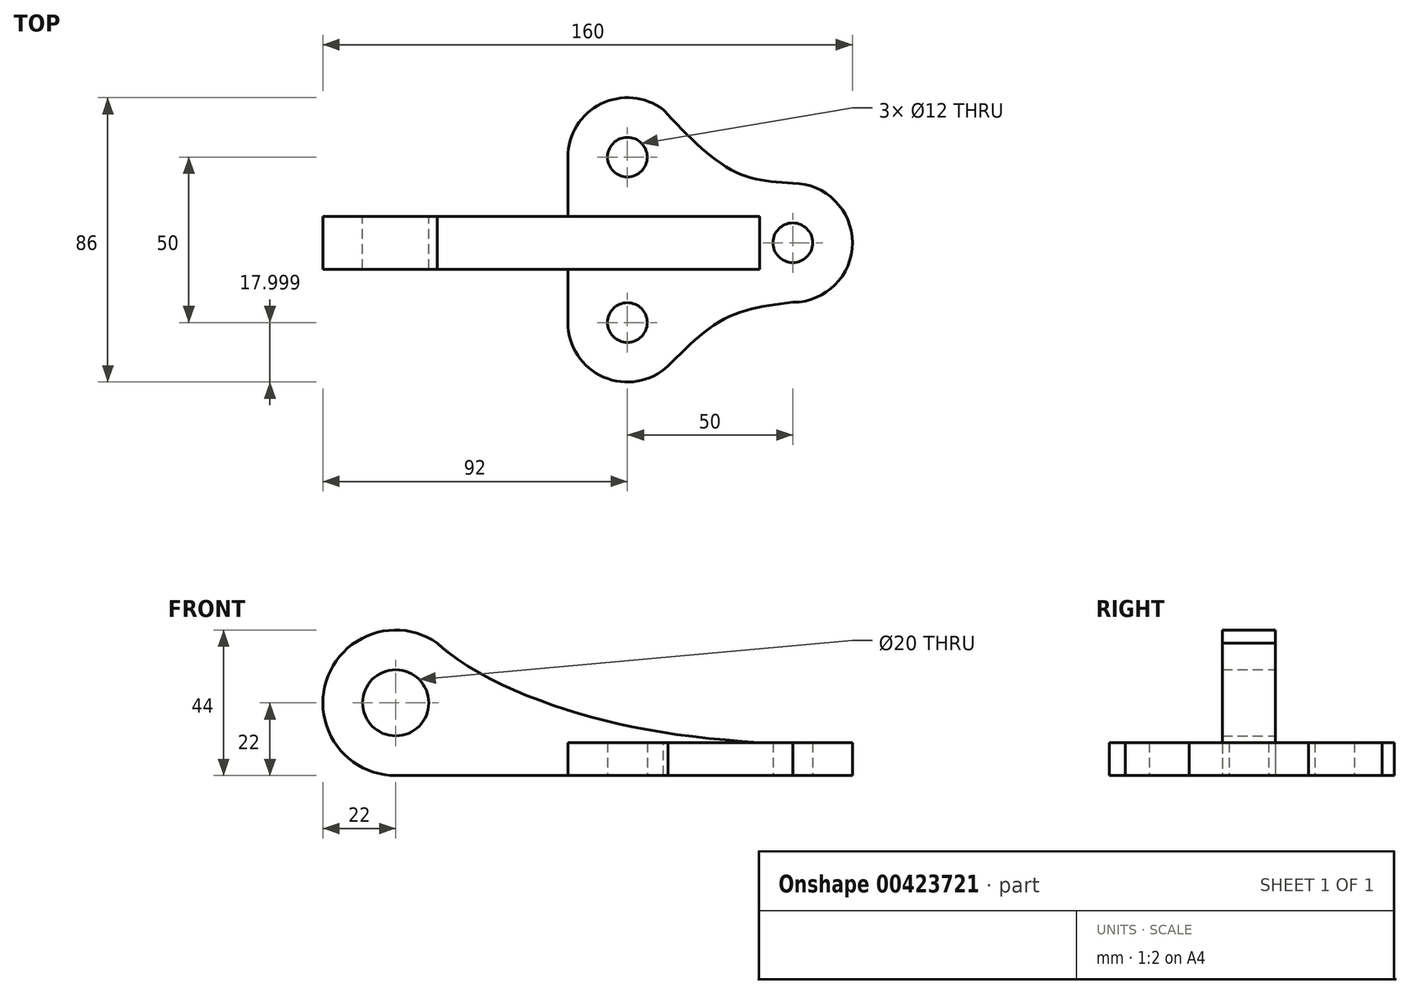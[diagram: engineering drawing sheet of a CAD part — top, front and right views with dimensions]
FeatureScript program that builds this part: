
annotation { "Feature Type Name" : "Feature", "Feature Type Description" : "" }
export const myFeature = defineFeature(function(context is Context, id is Id, definition is map)
    precondition{}
    {
        {
            var Q0;
            Q0=qCreatedBy(makeId("Top.planeOp"),FACE);
            var sketch = newSketch(context, id + "F0", { "sketchPlane" : qUnion([Q0])});
            skCircle(sketch, "E0", {"center": v(0, 25.88) * mm, "radius": 6 * mm});
            skCircle(sketch, "E1", {"center": v(0, -24.12) * mm, "radius": 6 * mm});
            skCircle(sketch, "E2", {"center": v(50, 0) * mm, "radius": 6 * mm});
            skArc(sketch, "E3", {"start": v(15.04, 35.78) * mm, "mid": v(-5.17, 43.12) * mm, "end": v(-18, 25.88) * mm});
            skArc(sketch, "E4", {"start": v(-18, -24.12) * mm, "mid": v(-6.53, -40.9) * mm, "end": v(13.27, -36.29) * mm});
            skArc(sketch, "E5", {"start": v(50.04, -18) * mm, "mid": v(68, 0) * mm, "end": v(50.04, 18) * mm});
            skLineSegment(sketch, "E6", {"start": v(-18, 25.88) * mm, "end": v(-18, -24.12) * mm});
            skFitSpline(sketch, "E7", {"points": [v(10.85, 40.24) * mm, v(31.96, 21.78) * mm, v(50.04, 18) * mm], "startDerivative": vector(37.97, -41.15) * mm, "endDerivative": vector(44.65, -2.57) * mm});
            skFitSpline(sketch, "E8", {"points": [v(12.28, -37.28) * mm, v(30.04, -22.69) * mm, v(50.04, -18) * mm], "startDerivative": vector(32.88, 33.18) * mm, "endDerivative": vector(42.76, 5.1) * mm});
            skSolve(sketch);
        }
        {
            var Q0;
            Q0=makeQuery(id+"F0.imprint","IMPRINT",FACE,{"disambiguationData":[TD([[makeQuery(id+"F0.imprint","IMPRINT",EDGE,{"derivedFrom":sQuery(id+"F0.wireOp",EDGE,"E0")}),-1.0]])]});
            extrude(context, id + "F1", {"entities" : qUnion([Q0]), "depth" : 10 * mm});
        }
        {
            var Q0;
            Q0=qCreatedBy(makeId("Front.planeOp"),FACE);
            var sketch = newSketch(context, id + "F2", { "sketchPlane" : qUnion([Q0])});
            skLineSegment(sketch, "E9", {"start": v(40, 0) * mm, "end": v(40, 10) * mm});
            skCircle(sketch, "E10", {"center": v(-70, 22) * mm, "radius": 10 * mm});
            skArc(sketch, "E11", {"start": v(-52.23, 34.97) * mm, "mid": v(-53.14, 36.14) * mm, "end": v(-54.14, 37.24) * mm});
            skLineSegment(sketch, "E12", {"start": v(-70, 0) * mm, "end": v(40, 0) * mm});
            skFitSpline(sketch, "E13", {"points": [v(-57.45, 40.07) * mm, v(-19.05, 20.14) * mm, v(40, 10) * mm], "startDerivative": vector(58.52, -54.63) * mm, "endDerivative": vector(132.12, -8.22) * mm});
            skArc(sketch, "E14.trimOffspring", {"start": v(-57.45, 40.07) * mm, "mid": v(-91, 28.57) * mm, "end": v(-70, 0) * mm});
            skSolve(sketch);
        }
        {
            var Q0;
            Q0=makeQuery(id+"F2.imprint","IMPRINT",FACE,{"disambiguationData":[TD([[makeQuery(id+"F2.imprint","IMPRINT",EDGE,{"derivedFrom":sQuery(id+"F2.wireOp",EDGE,"E9")}),1.0]])]});
            extrude(context, id + "F3", {"entities" : qUnion([Q0]), "operationType" : NewBodyOperationType.ADD, "depth" : 8 * mm, "hasSecondDirection" : true, "secondDirectionOppositeDirection" : true, "secondDirectionDepth" : 8 * mm});
        }
    });
